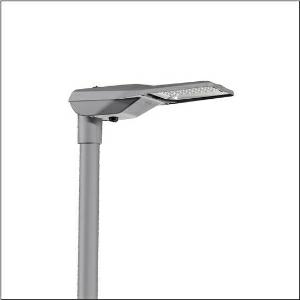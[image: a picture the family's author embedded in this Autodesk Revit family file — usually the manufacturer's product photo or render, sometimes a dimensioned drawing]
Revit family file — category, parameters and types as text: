
# Revit family: streetlight_sl_21_mini___st1_0a_5xe2d23t08hb_892b
name_source: partatom
category: Lighting Fixtures
units: mm (PartAtom-declared; Revit-internal decimal feet)

## family parameters
Cut with Voids When Loaded = No
Host = Face
Light Source = No
Part Type = Normal
Room Calculation Point = No
Round Connector Dimension = Use Diameter
Shared = No

## types (1)
- --- (1 x LED, 7490 lm, 66 W, 2200K)
    Apparent Load = 66 VA
    CIE Flux Codes = 37 72 97 100 100
    Color Rendering = 70
    Color Temperature = 2200K
    Default Elevation = 1800 mm
    Description = Streetlight SL 21 mini, mast luminaire, primary light control with lens, of PMMA, primary optical cover: cover, of toughened safety glass, transparent, light distribution: ST1.0a, light emission: direct distribution, primary light characteristic: asymmetric, installation type: side-entry, post-top, LED, High Power LED, rated luminous flux: 7.490lm, luminous efficacy: 114lm/W, light colour: 722, colour temperature: 2200K, control gear: D4i, control: overheat protection, constant luminous flux control, time-dependent luminous flux control, flexible luminous flux parameterisation, pre-setting: logarithmic dimming characteristic, mains connection: 220..240V, AC, 50/60Hz, start of lifetime: 66W, end of service life: 69W, reduction: 30W, luminaire housing, of diecast aluminium, powder-coated, SITECO metallic grey (DB 702S), corrosivity category C5 high according to DIN EN ISO 12944, please order mast flange separately, inclination adjustable: 0°, 5°, 10°, 15°, sealing non-destructively replaceable, multi-level sealing system, length: 628mm, width: 235mm, height: 110mm, mast flange for spigot size: 42mm (side-entry): 5XC10008XM4, 60/48mm (side-entry/post-top): 5XC10108XM2, 76/60mm (side-entry/post-top): 5XC10108XM1, mounting height: 4..8m, Smart Interface below and above, protection rating (complete): IP66, insulation class (complete): insulation class II (safety insulation), certification: CE, ENEC, ENEC+, VDE, impact resistance: IK10, permissible operating ambient temperature for outdoor applications: -40..+50°C, standard-compliant lighting for roads and squares, packaging unit: 1 piece

Light Distribution: ST1.0a
    Height = 110 mm
    Lamp = 1 x LED
    Lamp Light Flux = 7490 lm
    Lamp Power = 66 W
    Lamp count = 1
    Length = 625 mm
    Luminous efficacy = 113 lm/W
    Manufacturer = Siteco
    ModVariant = No
    Model = 5XE2D23T08HB
    Number of Poles = 1
    OnlyDefault = Yes
    Power Factor = 1
    Product Name = Streetlight SL 21 mini | ST1.0a
    Product group = mast luminaire | pylon top
    ProductGroupID = 6100
    Protection Class = Protection class II
    Protection Degree = IP 66
    RLX_Detail_Level = 1
    RLX_Emergency_Light_Flux = 0 lm
    RLX_Emergency_Type = 0
    RLX_Emergency_Type_DB = No
    RlxData = <blob elided: 26317 chars, md5=bff275fa>
    Socket = socket
    Standby Power = 0 W
    System Light Flux = 7490 lm
    System Power = 66 W
    Type Comments = factory setting: luminous flux: 100 % | dim-lin: 254 | 670 mA
    Type Image = l_1003514.jpg
    URL = http://relux.com
    VarID = @adj_185971
    Voltage = 0 V
    Weight = 0.00 kg
    Width = 234 mm

## geometry (parser evidence)
native form markers: Blend x4, Sweep x10
no freeform markers — native parametric forms only
